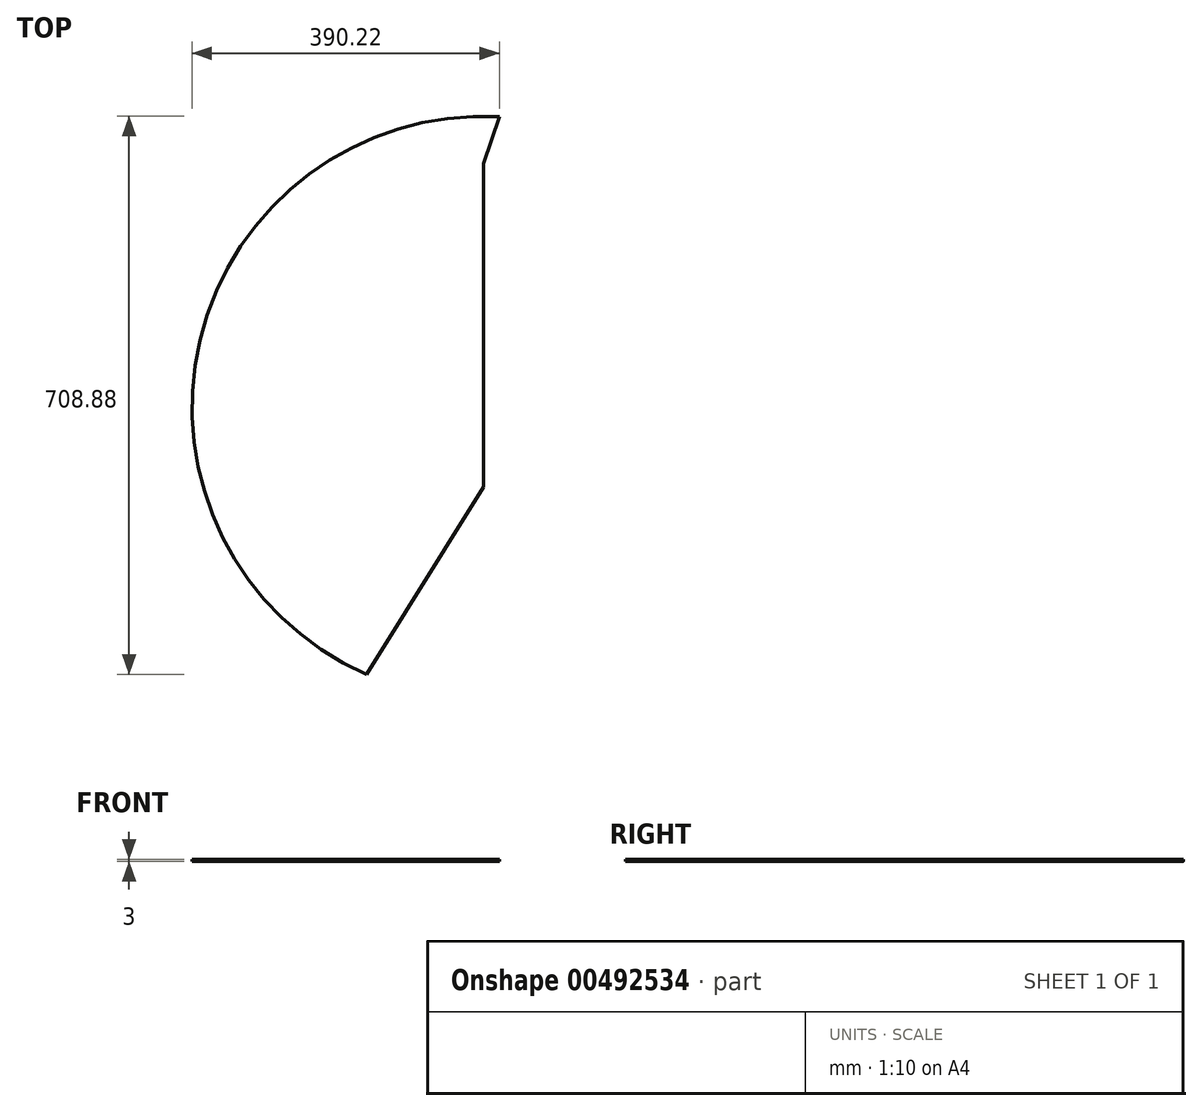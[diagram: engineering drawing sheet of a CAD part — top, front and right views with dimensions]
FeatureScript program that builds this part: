
annotation { "Feature Type Name" : "Feature", "Feature Type Description" : "" }
export const myFeature = defineFeature(function(context is Context, id is Id, definition is map)
    precondition{}
    {
        {
            var Q0;
            Q0=qCreatedBy(makeId("Top.planeOp"),FACE);
            var sketch = newSketch(context, id + "F0", { "sketchPlane" : qUnion([Q0])});
            skArc(sketch, "E0", {"start": v(2.35, 474.07) * mm, "mid": v(-377.8, 190.37) * mm, "end": v(-166.4, -234.26) * mm});
            skLineSegment(sketch, "E1", {"start": v(-17.87, 104.62) * mm, "end": v(-17.87, 414.62) * mm});
            skLineSegment(sketch, "E2", {"start": v(-17.87, 104.62) * mm, "end": v(-17.87, 3.66) * mm});
            skLineSegment(sketch, "E3", {"start": v(-17.87, 3.66) * mm, "end": v(-166.4, -234.26) * mm});
            skLineSegment(sketch, "E4", {"start": v(2.35, 474.07) * mm, "end": v(-17.87, 414.62) * mm});
            skSolve(sketch);
        }
        {
            var Q0;
            Q0=qSketchRegion(id+"F0",true);
            extrude(context, id + "F1", {"entities" : qUnion([Q0]), "depth" : 3 * mm});
        }
    });
